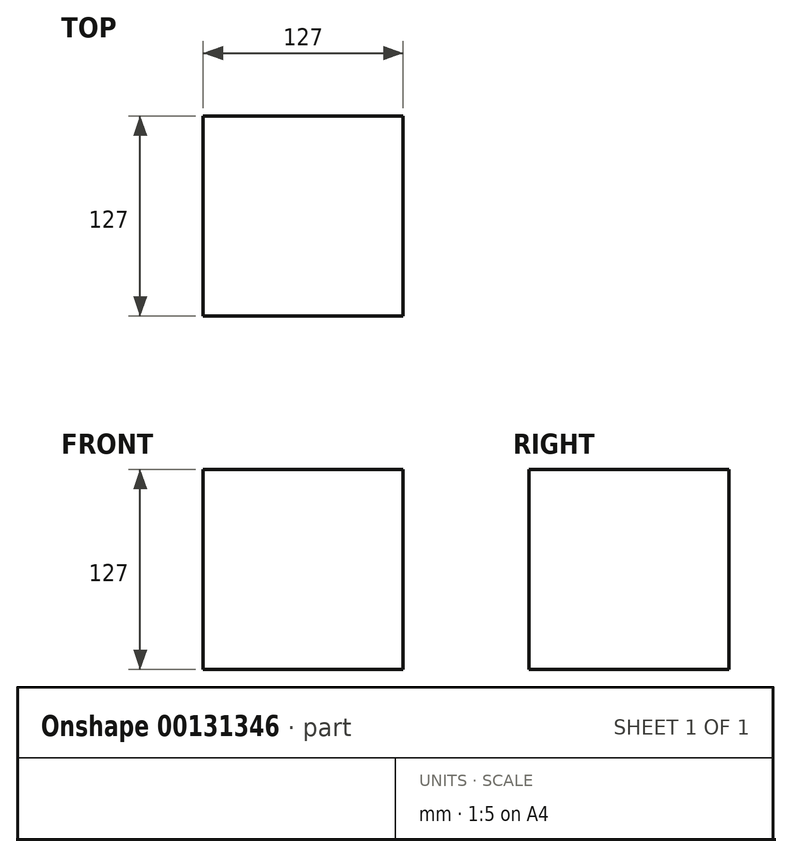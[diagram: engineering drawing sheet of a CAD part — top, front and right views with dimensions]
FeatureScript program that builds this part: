
annotation { "Feature Type Name" : "Feature", "Feature Type Description" : "" }
export const myFeature = defineFeature(function(context is Context, id is Id, definition is map)
    precondition{}
    {
        {
            var Q0;
            Q0=qCreatedBy(makeId("Front.planeOp"),FACE);
            var sketch = newSketch(context, id + "F0", { "sketchPlane" : qUnion([Q0])});
            skLineSegment(sketch, "E0.bottom", {"start": v(63.5, -63.5) * mm, "end": v(-63.5, -63.5) * mm});
            skLineSegment(sketch, "E0.top", {"start": v(63.5, 63.5) * mm, "end": v(-63.5, 63.5) * mm});
            skLineSegment(sketch, "E0.left", {"start": v(63.5, -63.5) * mm, "end": v(63.5, 63.5) * mm});
            skLineSegment(sketch, "E0.right", {"start": v(-63.5, -63.5) * mm, "end": v(-63.5, 63.5) * mm});
            skPoint(sketch, "E0.middle", {"position": v(0, 0) * mm});
            skSolve(sketch);
        }
        {
            var Q0;
            Q0=makeQuery(id+"F0.imprint","IMPRINT",FACE,{"disambiguationData":[TD([[makeQuery(id+"F0.imprint","IMPRINT",EDGE,{"derivedFrom":sQuery(id+"F0.wireOp",EDGE,"E0.bottom")}),-1.0]])]});
            extrude(context, id + "F1", {"entities" : qUnion([Q0]), "endBound" : BoundingType.SYMMETRIC, "depth" : 127 * mm});
        }
    });
